# Revit family: PRD_FrankeWS_SpprtRls_StraightGrabRail_CNTX300W_450W_600W_750W_900W_1050W_1100W
name_source: partatom
category: Specialty Equipment
revit_build: Autodesk Revit 2018 (Build: 20190510_1515(x64)
units: mm (PartAtom-declared; Revit-internal decimal feet)

## family parameters
Cut with Voids When Loaded = No
Host = Face
OmniClass Number = 23.40.20.21
OmniClass Title = Toilet and Bath Specialties
Part Type = Normal
Room Calculation Point = No
Round Connector Dimension = Use Diameter
Shared = No

## types (7) — shared parameters
AssetType = Fixed
BendingAngle = 0.00 degree
Category = Pr_40_20_76_84, Support rails
Color = no color
Default Elevation = 750 mm  [stored 2.46063 ft]
DurationUnit = year
Features = stainless steel, surface satin finished
Finish = satin finished
GrabRailMaterial = PRD_AR_StainlessSteel_SatinFinished
HiddenFixing = Yes
Hinged = No
IfcExportAs = IfcFurnitureType
IfcExportType = USERDEFINED
IntegralAccessories = incl. stainless steel screws and dowels
IsBuiltIn = TRUE
MainColor = stainless steel
Manufacturer = KWC Group AG
ManufacturerName = KWC Group AG
ManufacturerURL = www.kwc.com
Material = stainless steel
MaterialCode = 1.4301
MaterialThickness = 1.20 mm
NBSDescription = Support rails
NBSReference = 45-35-72/360
NominalDepth = 82 mm  [stored 0.269029 ft]
NominalHeight = 78 mm  [stored 0.255906 ft]
PipeDiameter = 32  [stored 0.104987 ft]
ProductInformation = https://pim.kwc.com
TypeOfFixing = Screw
TypeOfGrabRail = Straight bar
TypeOfMounting = Wall mounting
URL = www.kwc.com
Uniclass2015Code = Pr_40_20_76_84
Uniclass2015Title = Support rails
Uniclass2015Version = Products v1.10
Version = 1
WarrantyDurationUnit = year

## per-type parameters (varying)
| type | BIMObjectName | Back | Description | DistanceBetweenPoints | GrossWeight | ModelNumber | Name | NetWeight | NominalWidth | Size |
| CNTX600W | PRD_AR_SupportRails_StraightGrabRail_CNTX600W |  | Grab rail for wall mounting, stainless steel, surface satin finished, rough polishing for better surface feel, 32 mm pipe diameter, material thickness 1.2 mm, wall distance 82 mm, with two stainless steel covers for hidden mounting, includes stainless steel screws and dowels. Type 600 mm. | 600 mm | 1.21 kg | 2030032985 | Straight Grab Rail CNTX600W | 0.95 kg | 678 mm  [stored 2.22441 ft] | 678 x 78 x 82 mm |
| CNTX450W | PRD_AR_SupportRails_StraightGrabRail_CNTX450W |  | Grab rail for wall mounting, stainless steel, surface satin finished, rough polishing for better surface feel, 32 mm pipe diameter, material thickness 1.2 mm, wall distance 82 mm, with two stainless steel covers for hidden mounting, includes stainless steel screws and dowels. Type 450 mm. | 450 mm  [stored 1.47638 ft] | 1.10 kg | 2030033978 | Straight Grab Rail CNTX450W | 1.00 kg | 528 mm  [stored 1.73228 ft] | 528 x 78 x 82 mm |
| CNTX900W | PRD_AR_SupportRails_StraightGrabRail_CNTX900W |  | Grab rail for wall mounting, stainless steel, surface satin finished, rough polishing for better surface feel, 32 mm pipe diameter, material thickness 1.2 mm, wall distance 82 mm, with two stainless steel covers for hidden mounting, includes stainless steel screws and dowels. Type 900 mm. | 900 mm  [stored 2.95276 ft] | 2.32 kg | 2030033990 | Straight Grab Rail CNTX900W | 2.21 kg | 978 mm  [stored 3.20866 ft] | 978 x 78 x 82 mm |
| CNTX1100W | PRD_AR_SupportRails_StraightGrabRail_CNTX1100W |  | Grab rail for wall mounting, stainless steel, surface satin finished, rough polishing for better surface feel, 32 mm pipe diameter, material thickness 1.2 mm, wall distance 82 mm, with two stainless steel covers for hidden mounting, includes stainless steel screws and dowels. Type 1100 mm. | 1100 mm | 3.35 kg | 2030033994 | Straight Grab Rail CNTX1100W | 3.22 kg | 1178 mm | 1178 x 78 x 82 mm |
| CNTX300W | PRD_AR_SupportRails_StraightGrabRail_CNTX300W | No | Grab rail for wall mounting, stainless steel, surface satin finished, rough polishing for better surface feel, 32 mm pipe diameter, material thickness 1.2 mm, wall distance 82 mm, with two stainless steel covers for hidden mounting, includes stainless steel screws and dowels. Type 300 mm. | 300 mm | 0.89 kg | 2030033995 | Straight Grab Rail CNTX300W | 0.78 kg | 378 mm  [stored 1.24016 ft] | 378 x 78 x 82 mm |
| CNTX750W | PRD_AR_SupportRails_StraightGrabRail_CNTX750W |  | Grab rail for wall mounting, stainless steel, surface satin finished, rough polishing for better surface feel, 32 mm pipe diameter, material thickness 1.2 mm, wall distance 82 mm, with two stainless steel covers for hidden mounting, includes stainless steel screws and dowels. Type 750 mm. | 750 mm  [stored 2.46063 ft] | 1.52 kg | 2030033997 | Straight Grab Rail CNTX750W | 1.40 kg | 828 mm  [stored 2.71654 ft] | 828 x 78 x 82 mm |
| CNTX1050W | PRD_AR_SupportRails_StraightGrabRail_CNTX1050W | No | Straight grab rail for wall mounting, stainless steel, surface satin finished, rough polishing for better surface feel, 32 mm pipe diameter, material thickness 1.2 mm, wall distance 82 mm, with two stainless steel covers for hidden mounting, includes stainless steel screws and dowels. Type 1050 mm. | 1050 mm | 3.02 kg | 2030034502 | Straight Grab Rail CNTX1050W | 2.90 kg | 1128 mm | 1128 x 78 x 82 mm |

note: column(s) folded — value = type name in every type: Model, ModelReference

note: [stored X ft] marks values corroborated as IEEE doubles in the binary element streams (Revit-internal decimal feet)

## geometry (parser evidence)
native form markers: Sweep x4
no freeform markers — native parametric forms only
